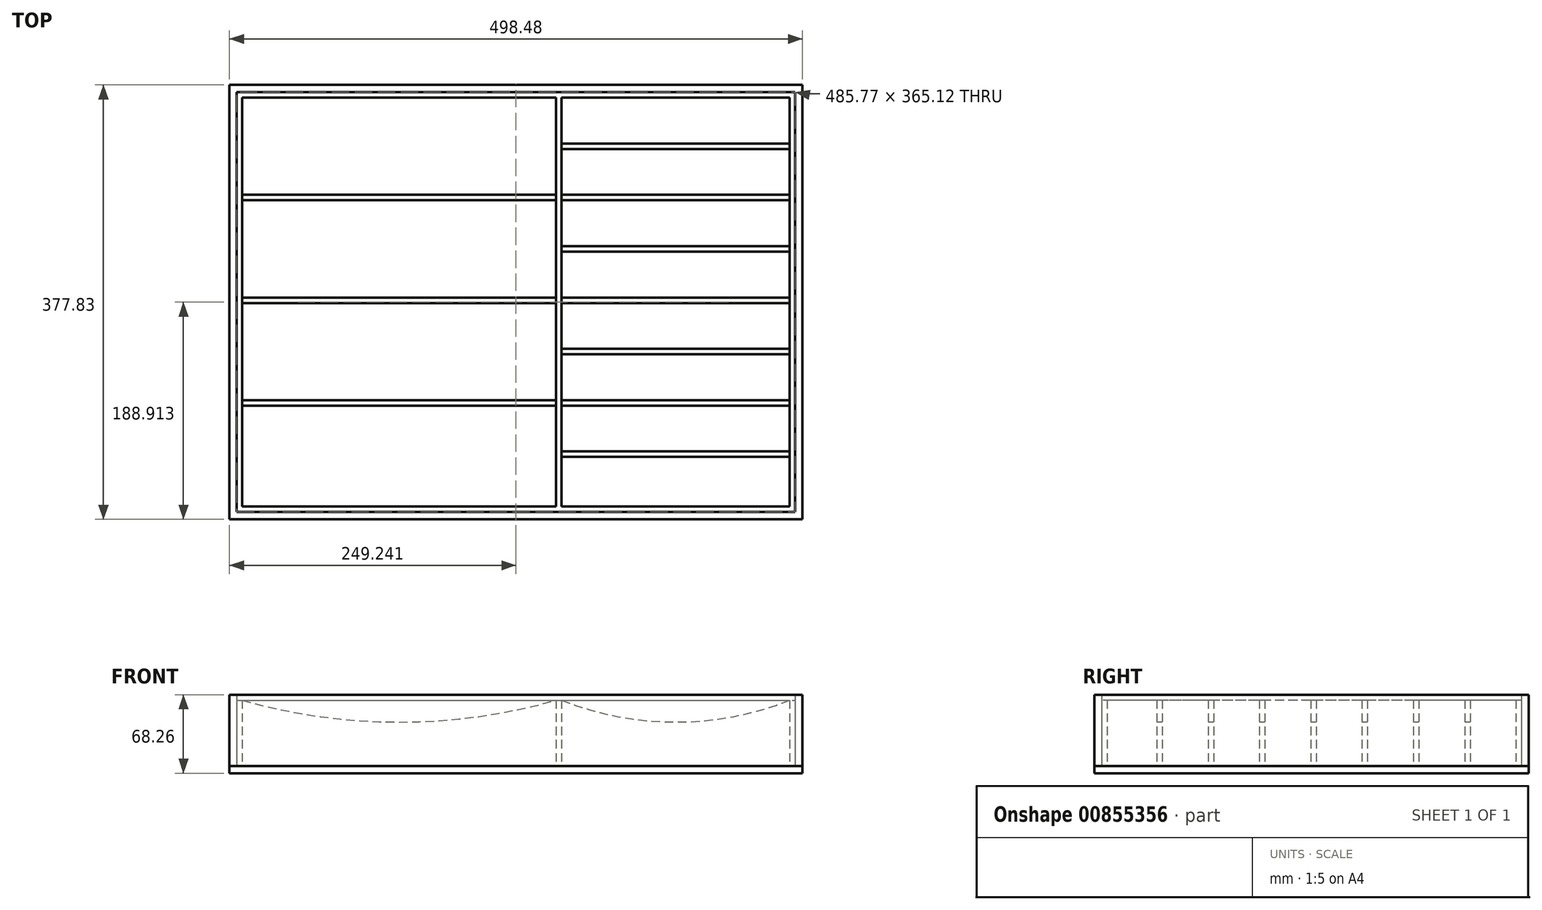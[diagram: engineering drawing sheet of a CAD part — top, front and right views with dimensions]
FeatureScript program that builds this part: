
annotation { "Feature Type Name" : "Feature", "Feature Type Description" : "" }
export const myFeature = defineFeature(function(context is Context, id is Id, definition is map)
    precondition{}
    {
        {
            var Q0;
            Q0=qCreatedBy(makeId("Top.planeOp"),FACE);
            var sketch = newSketch(context, id + "F0", { "sketchPlane" : qUnion([Q0])});
            skLineSegment(sketch, "E0.0", {"start": v(-250.52, 219.06) * mm, "end": v(-250.52, -146.07) * mm});
            skLineSegment(sketch, "E0.1", {"start": v(-250.52, 219.06) * mm, "end": v(235.26, 219.06) * mm});
            skLineSegment(sketch, "E0.2", {"start": v(235.26, 219.06) * mm, "end": v(235.26, -146.07) * mm});
            skLineSegment(sketch, "E0.3", {"start": v(-250.52, -146.07) * mm, "end": v(235.26, -146.07) * mm});
            skLineSegment(sketch, "E1.0", {"start": v(-245.75, 214.3) * mm, "end": v(-245.75, 129.78) * mm});
            skLineSegment(sketch, "E1.1", {"start": v(-245.75, 214.3) * mm, "end": v(27.3, 214.3) * mm});
            skLineSegment(sketch, "E1.2", {"start": v(230.5, 214.3) * mm, "end": v(230.5, 174.4) * mm});
            skLineSegment(sketch, "E2", {"start": v(-245.75, -141.3) * mm, "end": v(27.3, -141.3) * mm});
            skLineSegment(sketch, "E3", {"start": v(32.06, -141.3) * mm, "end": v(230.5, -141.3) * mm});
            skLineSegment(sketch, "E4", {"start": v(27.3, -141.3) * mm, "end": v(27.3, -53.5) * mm});
            skLineSegment(sketch, "E5", {"start": v(32.06, 214.3) * mm, "end": v(32.06, 174.4) * mm});
            skLineSegment(sketch, "E6.trimOffspring", {"start": v(32.06, 214.3) * mm, "end": v(230.5, 214.3) * mm});
            skLineSegment(sketch, "E7", {"start": v(32.06, -98.12) * mm, "end": v(230.5, -98.12) * mm});
            skLineSegment(sketch, "E8.0", {"start": v(32.06, -93.36) * mm, "end": v(230.5, -93.36) * mm});
            skLineSegment(sketch, "E9.0.1.0", {"start": v(32.06, -48.73) * mm, "end": v(230.5, -48.73) * mm});
            skLineSegment(sketch, "E9.0.1.1", {"start": v(32.06, -53.5) * mm, "end": v(230.5, -53.5) * mm});
            skLineSegment(sketch, "E9.0.2.0", {"start": v(32.06, -4.1) * mm, "end": v(230.5, -4.1) * mm});
            skLineSegment(sketch, "E9.0.2.1", {"start": v(32.06, -8.87) * mm, "end": v(230.5, -8.87) * mm});
            skLineSegment(sketch, "E9.0.3.0", {"start": v(32.06, 40.52) * mm, "end": v(230.5, 40.52) * mm});
            skLineSegment(sketch, "E9.0.3.1", {"start": v(32.06, 35.76) * mm, "end": v(230.5, 35.76) * mm});
            skLineSegment(sketch, "E9.0.4.0", {"start": v(32.06, 85.15) * mm, "end": v(230.5, 85.15) * mm});
            skLineSegment(sketch, "E9.0.4.1", {"start": v(32.06, 80.4) * mm, "end": v(230.5, 80.4) * mm});
            skLineSegment(sketch, "E9.0.5.0", {"start": v(32.06, 129.78) * mm, "end": v(230.5, 129.78) * mm});
            skLineSegment(sketch, "E9.0.5.1", {"start": v(32.06, 125.02) * mm, "end": v(230.5, 125.02) * mm});
            skLineSegment(sketch, "E9.0.6.0", {"start": v(32.06, 174.4) * mm, "end": v(230.5, 174.4) * mm});
            skLineSegment(sketch, "E9.0.6.1", {"start": v(32.06, 169.65) * mm, "end": v(230.5, 169.65) * mm});
            skLineSegment(sketch, "E9.direction1", {"start": v(32.06, -93.36) * mm, "end": v(57.46, -93.36) * mm, "construction": true});
            skLineSegment(sketch, "E9.direction2", {"start": v(32.06, -93.36) * mm, "end": v(32.06, -48.73) * mm, "construction": true});
            skLineSegment(sketch, "E10", {"start": v(27.3, -53.5) * mm, "end": v(-245.75, -53.5) * mm});
            skLineSegment(sketch, "E11", {"start": v(27.3, 35.76) * mm, "end": v(-245.75, 35.76) * mm});
            skLineSegment(sketch, "E12", {"start": v(27.3, 125.02) * mm, "end": v(-245.75, 125.02) * mm});
            skLineSegment(sketch, "E13.0", {"start": v(27.3, -48.73) * mm, "end": v(-245.75, -48.73) * mm});
            skLineSegment(sketch, "E14.0", {"start": v(27.3, 40.52) * mm, "end": v(-245.75, 40.52) * mm});
            skLineSegment(sketch, "E15.0", {"start": v(27.3, 129.78) * mm, "end": v(-245.75, 129.78) * mm});
            skLineSegment(sketch, "E16.trimOffspring", {"start": v(-245.75, 125.02) * mm, "end": v(-245.75, 40.52) * mm});
            skLineSegment(sketch, "E17.trimOffspring", {"start": v(-245.75, 35.76) * mm, "end": v(-245.75, -48.73) * mm});
            skLineSegment(sketch, "E18.trimOffspring", {"start": v(-245.75, -53.5) * mm, "end": v(-245.75, -141.3) * mm});
            skLineSegment(sketch, "E19.trimOffspring", {"start": v(32.06, -98.12) * mm, "end": v(32.06, -141.3) * mm});
            skLineSegment(sketch, "E20.trimOffspring", {"start": v(32.06, -53.5) * mm, "end": v(32.06, -93.36) * mm});
            skLineSegment(sketch, "E21.trimOffspring", {"start": v(27.3, -48.73) * mm, "end": v(27.3, 35.76) * mm});
            skLineSegment(sketch, "E22.trimOffspring", {"start": v(32.06, -8.87) * mm, "end": v(32.06, -48.73) * mm});
            skLineSegment(sketch, "E23.trimOffspring", {"start": v(32.06, 35.76) * mm, "end": v(32.06, -4.1) * mm});
            skLineSegment(sketch, "E24.trimOffspring", {"start": v(27.3, 40.52) * mm, "end": v(27.3, 125.02) * mm});
            skLineSegment(sketch, "E25.trimOffspring", {"start": v(32.06, 80.4) * mm, "end": v(32.06, 40.52) * mm});
            skLineSegment(sketch, "E26.trimOffspring", {"start": v(32.06, 125.02) * mm, "end": v(32.06, 85.15) * mm});
            skLineSegment(sketch, "E27.trimOffspring", {"start": v(27.3, 129.78) * mm, "end": v(27.3, 214.3) * mm});
            skLineSegment(sketch, "E28.trimOffspring", {"start": v(32.06, 169.65) * mm, "end": v(32.06, 129.78) * mm});
            skLineSegment(sketch, "E29.trimOffspring", {"start": v(230.5, 169.65) * mm, "end": v(230.5, 129.78) * mm});
            skLineSegment(sketch, "E30.trimOffspring", {"start": v(230.5, 125.02) * mm, "end": v(230.5, 85.15) * mm});
            skLineSegment(sketch, "E31.trimOffspring", {"start": v(230.5, 80.4) * mm, "end": v(230.5, 40.52) * mm});
            skLineSegment(sketch, "E32.trimOffspring", {"start": v(230.5, 35.76) * mm, "end": v(230.5, -4.1) * mm});
            skLineSegment(sketch, "E33.trimOffspring", {"start": v(230.5, -8.87) * mm, "end": v(230.5, -141.3) * mm});
            skLineSegment(sketch, "E34.0", {"start": v(-256.87, -152.42) * mm, "end": v(241.6, -152.42) * mm});
            skLineSegment(sketch, "E34.1", {"start": v(-256.87, 225.4) * mm, "end": v(-256.87, -152.42) * mm});
            skLineSegment(sketch, "E34.2", {"start": v(-256.87, 225.4) * mm, "end": v(241.6, 225.4) * mm});
            skLineSegment(sketch, "E34.3", {"start": v(241.6, 225.4) * mm, "end": v(241.6, -152.42) * mm});
            skSolve(sketch);
        }
        {
            var Q0;
            Q0=makeQuery(id+"F0.imprint","IMPRINT",FACE,{"disambiguationData":[TD([[makeQuery(id+"F0.imprint","IMPRINT",EDGE,{"derivedFrom":sQuery(id+"F0.wireOp",EDGE,"E0.0")}),1.0]])]});
            extrude(context, id + "F1", {"entities" : qUnion([Q0]), "depth" : 57.15 * mm, "offsetDistance" : 25.4 * mm});
        }
        {
            var Q0;
            Q0=makeQuery(id+"F0.imprint","IMPRINT",FACE,{"disambiguationData":[TD([[makeQuery(id+"F0.imprint","IMPRINT",EDGE,{"derivedFrom":sQuery(id+"F0.wireOp",EDGE,"E0.0")}),-1.0]])]});
            extrude(context, id + "F2", {"entities" : qUnion([Q0]), "depth" : 61.9 * mm, "offsetDistance" : 25.4 * mm});
        }
        {
            var Q0;
            Q0=makeQuery(id+"F0.imprint","IMPRINT",FACE,{"disambiguationData":[TD([[makeQuery(id+"F0.imprint","IMPRINT",EDGE,{"derivedFrom":sQuery(id+"F0.wireOp",EDGE,"E0.0")}),-1.0]])]});
            var sketch = newSketch(context, id + "F3", { "sketchPlane" : qUnion([Q0])});
            skPoint(sketch, "E35.0", {"position": v(-256.87, -152.42) * mm});
            skPoint(sketch, "E36.0", {"position": v(241.6, 225.4) * mm});
            skPoint(sketch, "E37.0", {"position": v(241.6, -152.42) * mm});
            skPoint(sketch, "E38.0", {"position": v(-256.87, 225.4) * mm});
            skLineSegment(sketch, "E39.bottom", {"start": v(-256.87, -152.42) * mm, "end": v(241.6, -152.42) * mm});
            skLineSegment(sketch, "E39.top", {"start": v(-256.87, 225.4) * mm, "end": v(241.6, 225.4) * mm});
            skLineSegment(sketch, "E39.left", {"start": v(-256.87, -152.42) * mm, "end": v(-256.87, 225.4) * mm});
            skLineSegment(sketch, "E39.right", {"start": v(241.6, -152.42) * mm, "end": v(241.6, 225.4) * mm});
            skSolve(sketch);
        }
        {
            var Q0;
            Q0=makeQuery(id+"F1.opExtrude","SWEPT_FACE",FACE,{"disambiguationData":[OSD([sQuery(id+"F0.wireOp",EDGE,"E2")])]});
            var sketch = newSketch(context, id + "F4", { "sketchPlane" : qUnion([Q0])});
            skLineSegment(sketch, "E40.0.0", {"start": v(-230.5, 0) * mm, "end": v(-32.06, 0) * mm});
            skLineSegment(sketch, "E40.0.1", {"start": v(-32.06, 0) * mm, "end": v(-32.06, 57.15) * mm});
            skLineSegment(sketch, "E40.0.2", {"start": v(-32.06, 57.15) * mm, "end": v(-230.5, 57.15) * mm});
            skLineSegment(sketch, "E40.0.3", {"start": v(-230.5, 57.15) * mm, "end": v(-230.5, 0) * mm});
            skArc(sketch, "E41", {"start": v(-230.5, 57.15) * mm, "mid": v(-131.28, 38.1) * mm, "end": v(-32.06, 57.15) * mm});
            skArc(sketch, "E42", {"start": v(-27.3, 57.15) * mm, "mid": v(109.23, 38.1) * mm, "end": v(245.75, 57.15) * mm});
            skLineSegment(sketch, "E43", {"start": v(-230.5, 57.15) * mm, "end": v(-32.06, 57.15) * mm});
            skLineSegment(sketch, "E44", {"start": v(-32.06, 57.15) * mm, "end": v(-27.3, 59.05) * mm});
            skLineSegment(sketch, "E45", {"start": v(-27.3, 59.05) * mm, "end": v(245.75, 57.15) * mm});
            skSolve(sketch);
        }
        {
            var Q0;
            Q0=makeQuery(id+"F4.imprint","IMPRINT",FACE,{"disambiguationData":[TD([[makeQuery(id+"F4.imprint","IMPRINT",EDGE,{"derivedFrom":sQuery(id+"F4.wireOp",EDGE,"E41")}),1.0]])]});
            var Q1;
            Q1=makeQuery(id+"F4.imprint","IMPRINT",FACE,{"disambiguationData":[TD([[makeQuery(id+"F4.imprint","IMPRINT",EDGE,{"derivedFrom":sQuery(id+"F4.wireOp",EDGE,"E42")}),1.0]])]});
            var Q2;
            Q2=makeQuery(id+"F1.opExtrude","SWEPT_FACE",FACE,{"disambiguationData":[OSD([sQuery(id+"F0.wireOp",EDGE,"E9.0.6.0")])]});
            extrude(context, id + "F5", {"entities" : qUnion([Q0, Q1]), "operationType" : NewBodyOperationType.REMOVE, "endBound" : BoundingType.UP_TO_SURFACE, "depth" : 25.4 * mm, "endBoundEntityFace" : qUnion([Q2]), "offsetDistance" : 25.4 * mm});
        }
        {
            var Q0;
            Q0 = qSketchRegion(id + "F3", true);
            extrude(context, id + "F6", {"entities" : qUnion([Q0]), "oppositeDirection" : true, "depth" : 6.35 * mm, "offsetDistance" : 25.4 * mm});
        }
    });
